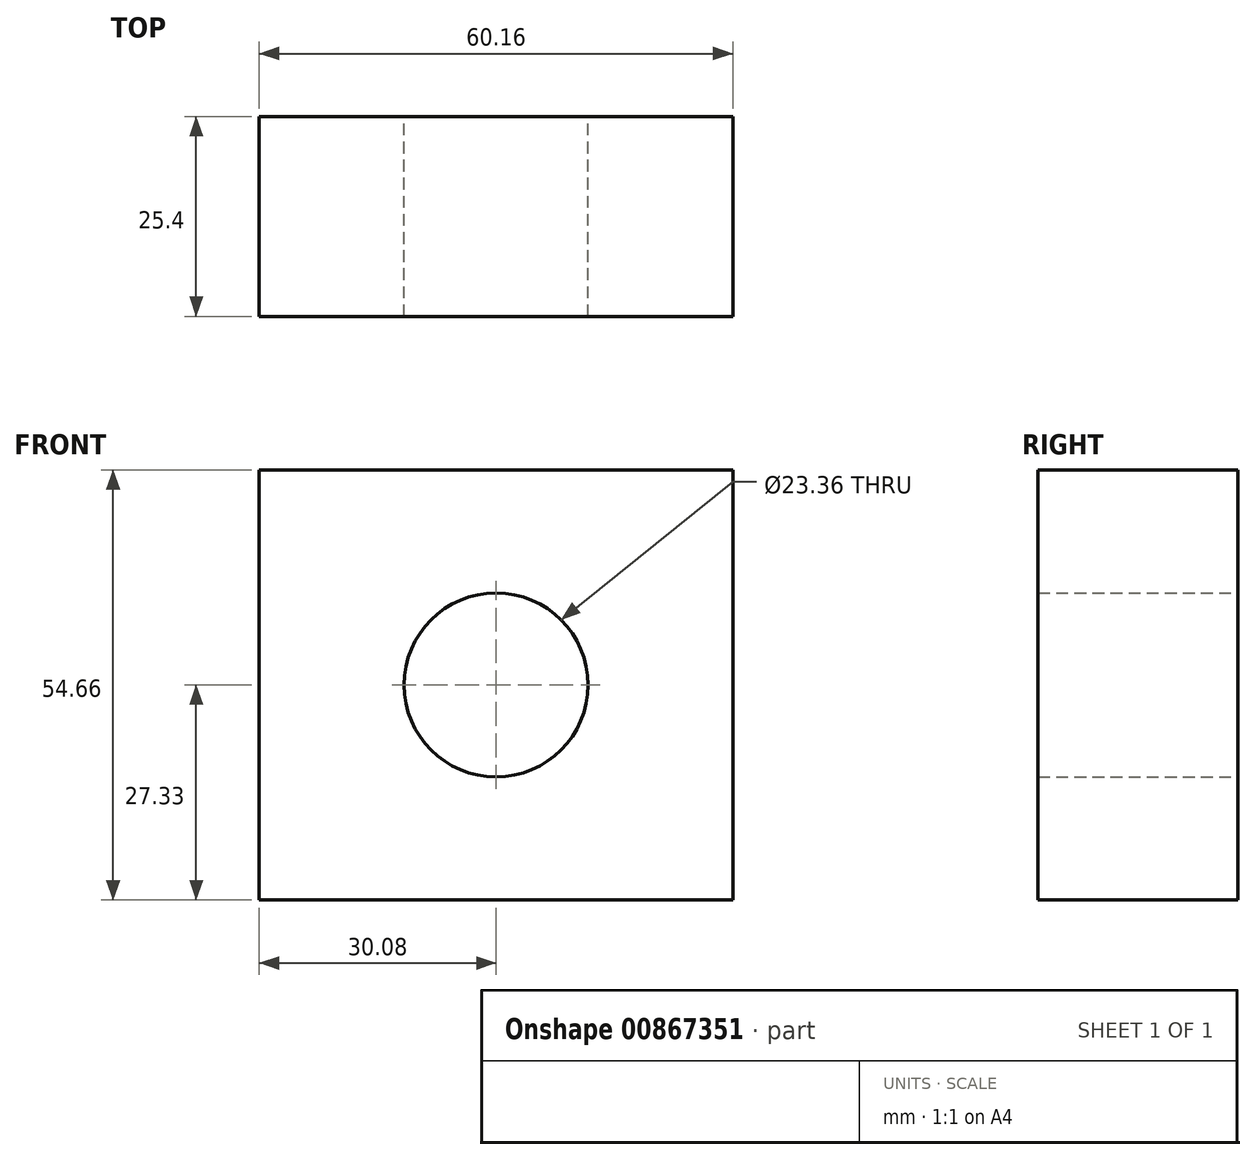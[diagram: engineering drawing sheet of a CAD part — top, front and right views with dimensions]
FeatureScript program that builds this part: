
annotation { "Feature Type Name" : "Feature", "Feature Type Description" : "" }
export const myFeature = defineFeature(function(context is Context, id is Id, definition is map)
    precondition{}
    {
        {
            var Q0;
            Q0=qCreatedBy(makeId("Front.planeOp"),FACE);
            var sketch = newSketch(context, id + "F0", { "sketchPlane" : qUnion([Q0])});
            skLineSegment(sketch, "E0.bottom", {"start": v(-30.08, 27.33) * mm, "end": v(30.08, 27.33) * mm});
            skLineSegment(sketch, "E0.top", {"start": v(-30.08, -27.33) * mm, "end": v(30.08, -27.33) * mm});
            skLineSegment(sketch, "E0.left", {"start": v(-30.08, 27.33) * mm, "end": v(-30.08, -27.33) * mm});
            skLineSegment(sketch, "E0.right", {"start": v(30.08, 27.33) * mm, "end": v(30.08, -27.33) * mm});
            skPoint(sketch, "E0.middle", {"position": v(0, 0) * mm});
            skCircle(sketch, "E1", {"center": v(0, 0) * mm, "radius": 11.68 * mm});
            skSolve(sketch);
        }
        {
            var Q0;
            Q0 = qSketchRegion(id + "F0", true);
            extrude(context, id + "F1", {"entities" : qUnion([Q0]), "depth" : 25.4 * mm, "offsetDistance" : 25.4 * mm});
        }
    });
